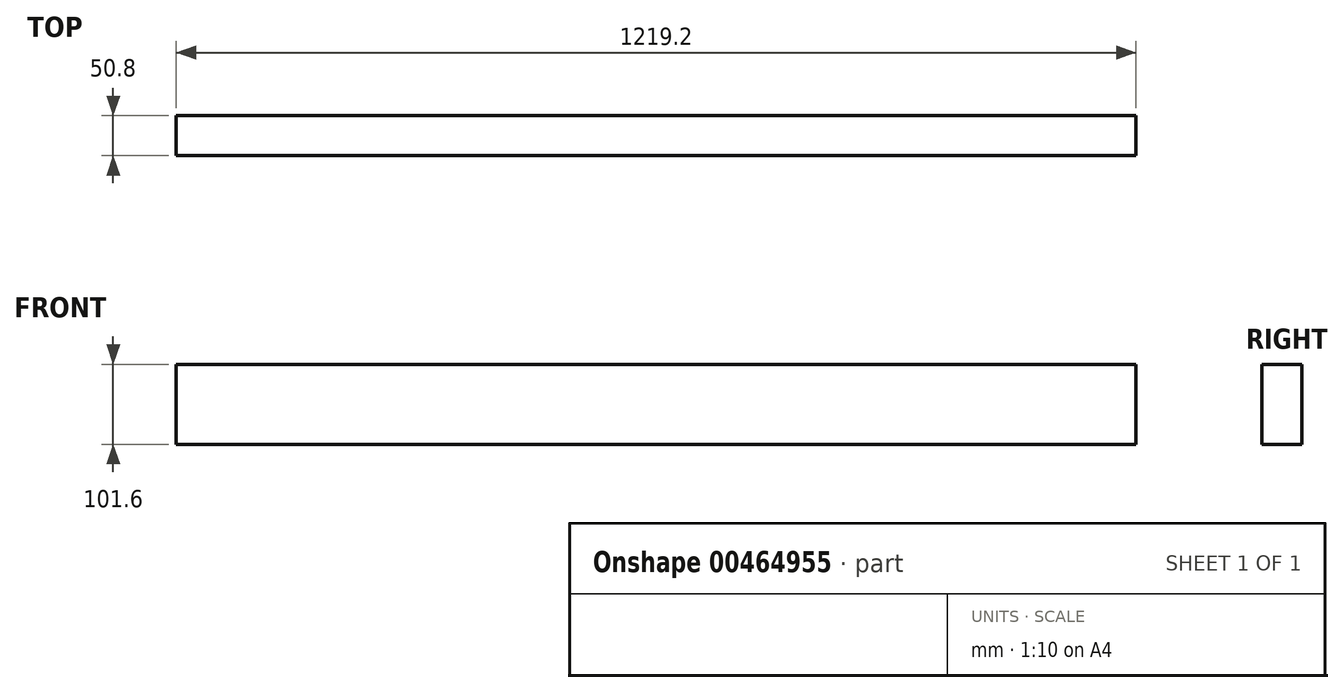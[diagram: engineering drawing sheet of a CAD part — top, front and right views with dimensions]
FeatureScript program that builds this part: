
annotation { "Feature Type Name" : "Feature", "Feature Type Description" : "" }
export const myFeature = defineFeature(function(context is Context, id is Id, definition is map)
    precondition{}
    {
        {
            var Q0;
            Q0=qCreatedBy(makeId("Top.planeOp"),FACE);
            var sketch = newSketch(context, id + "F0", { "sketchPlane" : qUnion([Q0])});
            skLineSegment(sketch, "E0.bottom", {"start": v(-609.6, -25.4) * mm, "end": v(609.6, -25.4) * mm});
            skLineSegment(sketch, "E0.top", {"start": v(-609.6, 25.4) * mm, "end": v(609.6, 25.4) * mm});
            skLineSegment(sketch, "E0.left", {"start": v(-609.6, -25.4) * mm, "end": v(-609.6, 25.4) * mm});
            skLineSegment(sketch, "E0.right", {"start": v(609.6, -25.4) * mm, "end": v(609.6, 25.4) * mm});
            skPoint(sketch, "E0.middle", {"position": v(0, 0) * mm});
            skSolve(sketch);
        }
        {
            var Q0;
            Q0 = qSketchRegion(id + "F0", true);
            extrude(context, id + "F1", {"entities" : qUnion([Q0]), "depth" : 101.6 * mm});
        }
    });
